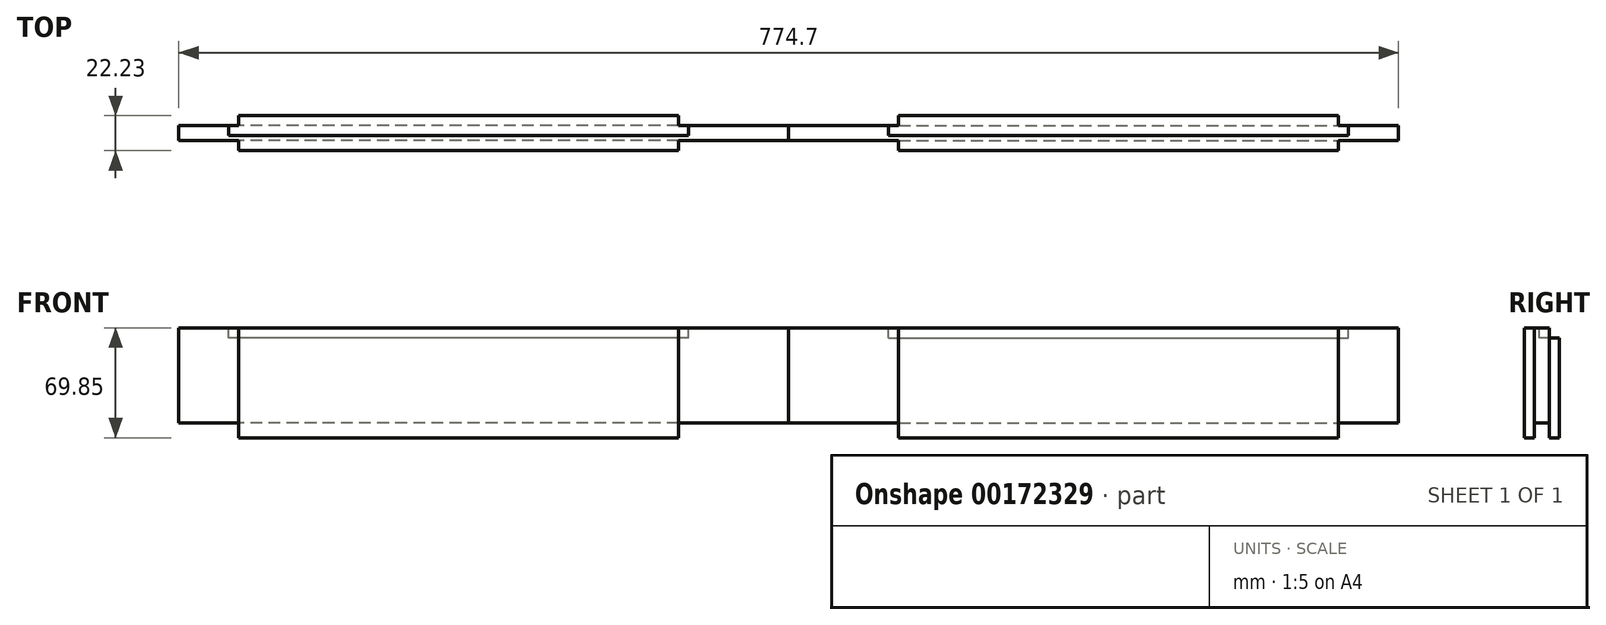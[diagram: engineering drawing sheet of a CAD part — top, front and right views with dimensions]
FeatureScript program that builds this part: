
annotation { "Feature Type Name" : "Feature", "Feature Type Description" : "" }
export const myFeature = defineFeature(function(context is Context, id is Id, definition is map)
    precondition{}
    {
        {
            var Q0;
            Q0=qCreatedBy(makeId("Front.planeOp"),FACE);
            var sketch = newSketch(context, id + "F0", { "sketchPlane" : qUnion([Q0])});
            skLineSegment(sketch, "E0.bottom", {"start": v(0, 0) * mm, "end": v(387.35, 0) * mm});
            skLineSegment(sketch, "E0.top", {"start": v(0, 69.85) * mm, "end": v(387.35, 69.85) * mm});
            skLineSegment(sketch, "E0.left", {"start": v(0, 0) * mm, "end": v(0, 69.85) * mm});
            skLineSegment(sketch, "E0.right", {"start": v(387.35, 0) * mm, "end": v(387.35, 69.85) * mm});
            skSolve(sketch);
        }
        {
            var Q0;
            Q0=makeQuery(id+"F0.imprint","IMPRINT",FACE,{"disambiguationData":[TD([[makeQuery(id+"F0.imprint","IMPRINT",EDGE,{"derivedFrom":sQuery(id+"F0.wireOp",EDGE,"E0.bottom")}),1.0]])]});
            extrude(context, id + "F1", {"entities" : qUnion([Q0]), "depth" : 22.22 * mm});
        }
        {
            var Q0;
            Q0=makeQuery(id+"F1.opExtrude","SWEPT_FACE",FACE,{"disambiguationData":[OSD([sQuery(id+"F0.wireOp",EDGE,"E0.bottom")])]});
            var sketch = newSketch(context, id + "F2", { "sketchPlane" : qUnion([Q0])});
            skLineSegment(sketch, "E1.bottom", {"start": v(0, 15.88) * mm, "end": v(387.35, 15.88) * mm});
            skLineSegment(sketch, "E1.top", {"start": v(0, 6.35) * mm, "end": v(387.35, 6.35) * mm});
            skLineSegment(sketch, "E1.left", {"start": v(0, 15.88) * mm, "end": v(0, 6.35) * mm});
            skLineSegment(sketch, "E1.right", {"start": v(387.35, 15.88) * mm, "end": v(387.35, 6.35) * mm});
            skLineSegment(sketch, "E2", {"start": v(69.85, 0) * mm, "end": v(69.85, 22.23) * mm});
            skLineSegment(sketch, "E3", {"start": v(349.25, 22.23) * mm, "end": v(349.25, 0) * mm});
            skSolve(sketch);
        }
        {
            var Q0;
            {var subQ1=sQuery(id+"F0.wireOp",EDGE,"E0.bottom");var subQ4=sQuery(id+"F2.wireOp",EDGE,"E2");var subQ6=makeQuery(id+"F1.opExtrude","CAP_EDGE",EDGE,{"disambiguationData":[OSD([subQ1])],"isStart":false});var subQ7=makeQuery(id+"F2.imprint","INTERSECT",VERTEX,{"derivedFrom":[subQ6,subQ4]});Q0=makeQuery(id+"F2.imprint","IMPRINT",FACE,{"disambiguationData":[TD([[makeQuery(id+"F2.imprint","IMPRINT",EDGE,{"disambiguationData":[TD([[subQ7,1.0]])],"derivedFrom":subQ4}),1.0]])]});}
            var Q1;
            {var subQ1=sQuery(id+"F0.wireOp",EDGE,"E0.bottom");var subQ4=sQuery(id+"F2.wireOp",EDGE,"E2");var subQ6=makeQuery(id+"F1.opExtrude","CAP_EDGE",EDGE,{"disambiguationData":[OSD([subQ1])],"isStart":true});var subQ7=makeQuery(id+"F2.imprint","INTERSECT",VERTEX,{"derivedFrom":[subQ6,subQ4]});Q1=makeQuery(id+"F2.imprint","IMPRINT",FACE,{"disambiguationData":[TD([[makeQuery(id+"F2.imprint","IMPRINT",EDGE,{"disambiguationData":[TD([[subQ7,-1.0]])],"derivedFrom":subQ4}),1.0]])]});}
            var Q2;
            {var subQ1=sQuery(id+"F0.wireOp",EDGE,"E0.bottom");var subQ4=sQuery(id+"F2.wireOp",EDGE,"E3");var subQ6=makeQuery(id+"F1.opExtrude","CAP_EDGE",EDGE,{"disambiguationData":[OSD([subQ1])],"isStart":false});var subQ7=makeQuery(id+"F2.imprint","INTERSECT",VERTEX,{"derivedFrom":[subQ6,subQ4]});Q2=makeQuery(id+"F2.imprint","IMPRINT",FACE,{"disambiguationData":[TD([[makeQuery(id+"F2.imprint","IMPRINT",EDGE,{"disambiguationData":[TD([[subQ7,-1.0]])],"derivedFrom":subQ4}),1.0]])]});}
            var Q3;
            {var subQ1=sQuery(id+"F0.wireOp",EDGE,"E0.bottom");var subQ4=sQuery(id+"F2.wireOp",EDGE,"E3");var subQ6=makeQuery(id+"F1.opExtrude","CAP_EDGE",EDGE,{"disambiguationData":[OSD([subQ1])],"isStart":true});var subQ7=makeQuery(id+"F2.imprint","INTERSECT",VERTEX,{"derivedFrom":[subQ6,subQ4]});Q3=makeQuery(id+"F2.imprint","IMPRINT",FACE,{"disambiguationData":[TD([[makeQuery(id+"F2.imprint","IMPRINT",EDGE,{"disambiguationData":[TD([[subQ7,1.0]])],"derivedFrom":subQ4}),1.0]])]});}
            extrude(context, id + "F3", {"entities" : qUnion([Q0, Q1, Q2, Q3]), "operationType" : NewBodyOperationType.REMOVE, "endBound" : BoundingType.UP_TO_NEXT, "oppositeDirection" : true, "depth" : 25.4 * mm});
        }
        {
            var Q0;
            {var subQ0=sQuery(id+"F2.wireOp",EDGE,"E1.left");Q0=makeQuery(id+"F2.imprint","IMPRINT",FACE,{"disambiguationData":[TD([[makeQuery(id+"F2.imprint","IMPRINT",EDGE,{"derivedFrom":subQ0}),1.0]])]});}
            var Q1;
            {var subQ0=sQuery(id+"F2.wireOp",EDGE,"E2");var subQ1=sQuery(id+"F2.wireOp",EDGE,"E1.bottom");var subQ2=makeQuery(id+"F2.imprint","INTERSECT",VERTEX,{"derivedFrom":[subQ1,subQ0]});Q1=makeQuery(id+"F2.imprint","IMPRINT",FACE,{"disambiguationData":[TD([[makeQuery(id+"F2.imprint","IMPRINT",EDGE,{"disambiguationData":[TD([[subQ2,-1.0]])],"derivedFrom":subQ1}),-1.0]])]});}
            var Q2;
            {var subQ0=sQuery(id+"F2.wireOp",EDGE,"E1.right");Q2=makeQuery(id+"F2.imprint","IMPRINT",FACE,{"disambiguationData":[TD([[makeQuery(id+"F2.imprint","IMPRINT",EDGE,{"derivedFrom":subQ0}),-1.0]])]});}
            extrude(context, id + "F4", {"entities" : qUnion([Q0, Q1, Q2]), "operationType" : NewBodyOperationType.REMOVE, "oppositeDirection" : true, "depth" : 9.52 * mm});
        }
        {
            var Q0;
            Q0=makeQuery(id+"F1.opExtrude","SWEPT_FACE",FACE,{"disambiguationData":[OSD([sQuery(id+"F0.wireOp",EDGE,"E0.top")])]});
            var sketch = newSketch(context, id + "F5", { "sketchPlane" : qUnion([Q0])});
            skLineSegment(sketch, "E4.bottom", {"start": v(63.5, 0) * mm, "end": v(355.6, 0) * mm});
            skLineSegment(sketch, "E4.top", {"start": v(63.5, -12.7) * mm, "end": v(355.6, -12.7) * mm});
            skLineSegment(sketch, "E4.left", {"start": v(63.5, 0) * mm, "end": v(63.5, -12.7) * mm});
            skLineSegment(sketch, "E4.right", {"start": v(355.6, 0) * mm, "end": v(355.6, -12.7) * mm});
            skSolve(sketch);
        }
        {
            var Q0;
            {var subQ1=sQuery(id+"F5.wireOp",EDGE,"E4.top");Q0=makeQuery(id+"F5.imprint","IMPRINT",FACE,{"disambiguationData":[TD([[makeQuery(id+"F5.imprint","IMPRINT",EDGE,{"derivedFrom":subQ1}),1.0]])]});}
            extrude(context, id + "F6", {"entities" : qUnion([Q0]), "operationType" : NewBodyOperationType.REMOVE, "oppositeDirection" : true, "depth" : 6.35 * mm});
        }
        {
            var Q0;
            Q0=makeQuery(id+"F1.opExtrude","SWEPT_BODY",BODY,{"disambiguationData":[OSD([sQuery(id+"F0.wireOp",EDGE,"E0.bottom"),sQuery(id+"F0.wireOp",EDGE,"E0.top"),sQuery(id+"F0.wireOp",EDGE,"E0.left"),sQuery(id+"F0.wireOp",EDGE,"E0.right")])]});
            var Q1;
            Q1=qCreatedBy(makeId("Right.planeOp"),FACE);
            mirror(context, id + "F7", {"entities" : qUnion([Q0]), "mirrorPlane" : qUnion([Q1])});
        }
    });
